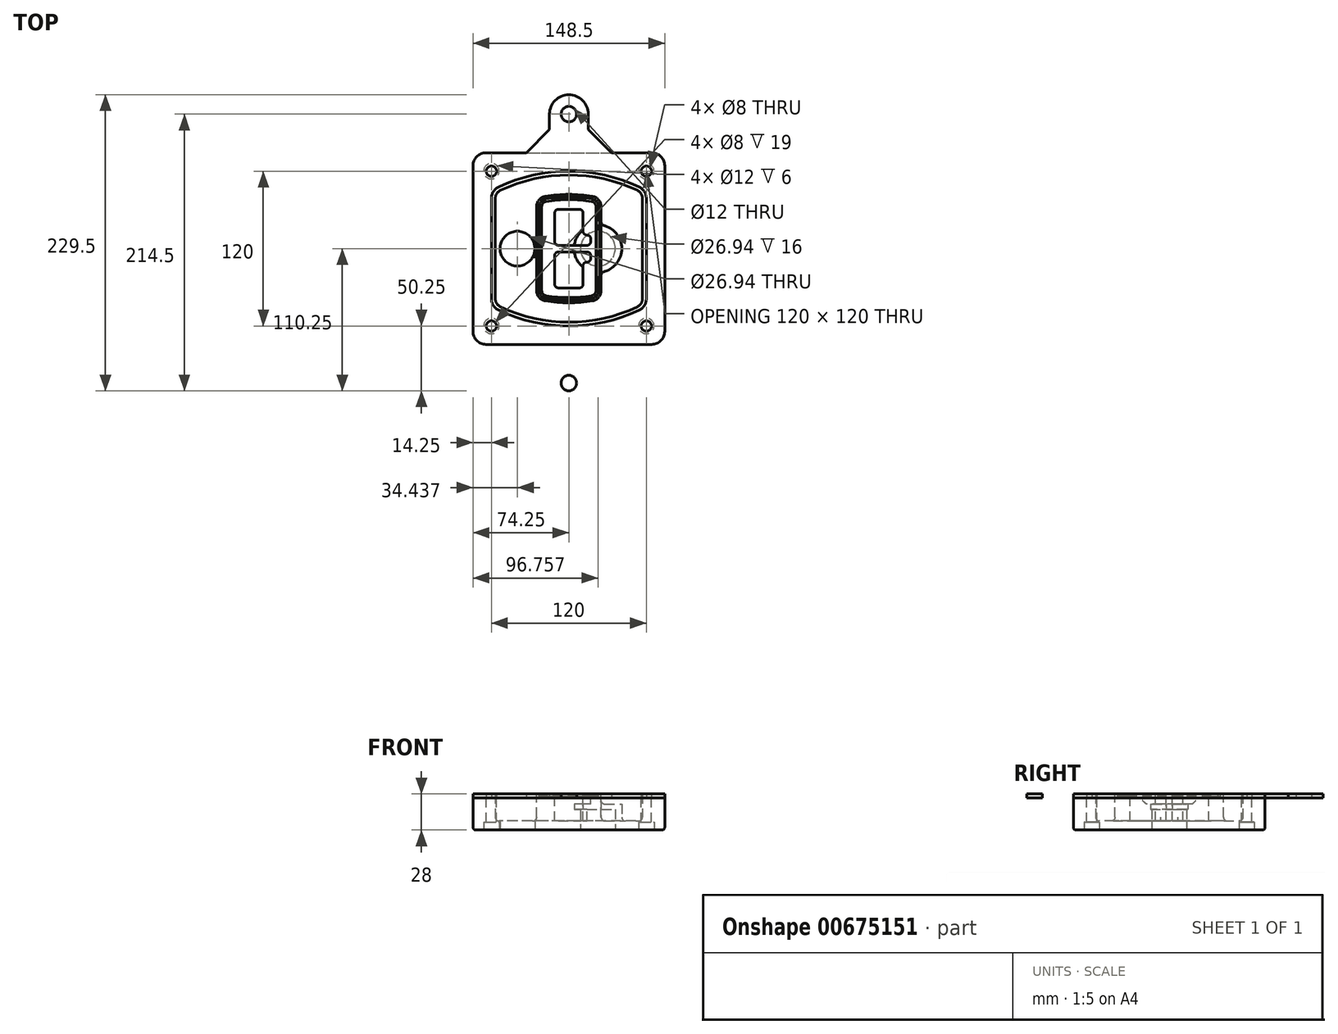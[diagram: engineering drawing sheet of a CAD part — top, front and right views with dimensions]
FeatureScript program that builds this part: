
annotation { "Feature Type Name" : "Feature", "Feature Type Description" : "" }
export const myFeature = defineFeature(function(context is Context, id is Id, definition is map)
    precondition{}
    {
        {
            var Q0;
            Q0=qCreatedBy(makeId("Top.planeOp"),FACE);
            var sketch = newSketch(context, id + "F0", { "sketchPlane" : qUnion([Q0])});
            skPoint(sketch, "E0.rect.middle", {"position": v(0, 0) * mm});
            skLineSegment(sketch, "E1.bottom", {"start": v(-64.25, -74.25) * mm, "end": v(64.25, -74.25) * mm});
            skLineSegment(sketch, "E1.top", {"start": v(-64.25, 74.25) * mm, "end": v(64.25, 74.25) * mm});
            skLineSegment(sketch, "E1.left", {"start": v(-74.25, -64.25) * mm, "end": v(-74.25, 64.25) * mm});
            skLineSegment(sketch, "E1.right", {"start": v(74.25, -64.25) * mm, "end": v(74.25, 64.25) * mm});
            skLineSegment(sketch, "E2", {"start": v(-74.25, 74.25) * mm, "end": v(74.25, -74.25) * mm, "construction": true});
            skLineSegment(sketch, "E3", {"start": v(74.25, 74.25) * mm, "end": v(-74.25, -74.25) * mm, "construction": true});
            skCircle(sketch, "E4", {"center": v(-60, 60) * mm, "radius": 4 * mm});
            skCircle(sketch, "E5", {"center": v(60, 60) * mm, "radius": 4 * mm});
            skCircle(sketch, "E6", {"center": v(60, -60) * mm, "radius": 4 * mm});
            skCircle(sketch, "E7", {"center": v(-60, -60) * mm, "radius": 4 * mm});
            skLineSegment(sketch, "E8", {"start": v(-60, 60) * mm, "end": v(60, 60) * mm, "construction": true});
            skLineSegment(sketch, "E9", {"start": v(60, 60) * mm, "end": v(60, -60) * mm, "construction": true});
            skLineSegment(sketch, "E10", {"start": v(60, -60) * mm, "end": v(-60, -60) * mm, "construction": true});
            skLineSegment(sketch, "E11", {"start": v(-60, -60) * mm, "end": v(-60, 60) * mm, "construction": true});
            skLineSegment(sketch, "E12", {"start": v(-60, 38.83) * mm, "end": v(-60, -38.83) * mm});
            skLineSegment(sketch, "E13", {"start": v(60, 38.83) * mm, "end": v(60, -38.83) * mm});
            skArc(sketch, "E14", {"start": v(54.26, 47.88) * mm, "mid": v(0, 60) * mm, "end": v(-54.26, 47.88) * mm});
            skArc(sketch, "E15", {"start": v(-54.26, -47.88) * mm, "mid": v(0, -60) * mm, "end": v(54.26, -47.88) * mm});
            skLineSegment(sketch, "E16", {"start": v(-60, 0) * mm, "end": v(60, 0) * mm, "construction": true});
            skPoint(sketch, "E17.visualSharp", {"position": v(-60, -45) * mm});
            skArc(sketch, "E17.filletArc", {"start": v(-60, -38.83) * mm, "mid": v(-58.44, -44.2) * mm, "end": v(-54.26, -47.88) * mm});
            skPoint(sketch, "E18.visualSharp", {"position": v(-60, 45) * mm});
            skArc(sketch, "E18.filletArc", {"start": v(-54.26, 47.88) * mm, "mid": v(-58.44, 44.2) * mm, "end": v(-60, 38.83) * mm});
            skPoint(sketch, "E19.visualSharp", {"position": v(60, 45) * mm});
            skArc(sketch, "E19.filletArc", {"start": v(60, 38.83) * mm, "mid": v(58.44, 44.2) * mm, "end": v(54.26, 47.88) * mm});
            skPoint(sketch, "E20.visualSharp", {"position": v(60, -45) * mm});
            skArc(sketch, "E20.filletArc", {"start": v(54.26, -47.88) * mm, "mid": v(58.44, -44.2) * mm, "end": v(60, -38.83) * mm});
            skPoint(sketch, "E21.visualSharp", {"position": v(-74.25, 74.25) * mm});
            skArc(sketch, "E21.filletArc", {"start": v(-64.25, 74.25) * mm, "mid": v(-71.32, 71.32) * mm, "end": v(-74.25, 64.25) * mm});
            skPoint(sketch, "E22.visualSharp", {"position": v(74.25, 74.25) * mm});
            skArc(sketch, "E22.filletArc", {"start": v(74.25, 64.25) * mm, "mid": v(71.32, 71.32) * mm, "end": v(64.25, 74.25) * mm});
            skPoint(sketch, "E23.visualSharp", {"position": v(74.25, -74.25) * mm});
            skArc(sketch, "E23.filletArc", {"start": v(64.25, -74.25) * mm, "mid": v(71.32, -71.32) * mm, "end": v(74.25, -64.25) * mm});
            skPoint(sketch, "E24.visualSharp", {"position": v(-74.25, -74.25) * mm});
            skArc(sketch, "E24.filletArc", {"start": v(-74.25, -64.25) * mm, "mid": v(-71.32, -71.32) * mm, "end": v(-64.25, -74.25) * mm});
            skArc(sketch, "E25.0", {"start": v(57, 38.83) * mm, "mid": v(55.9, 42.58) * mm, "end": v(52.98, 45.17) * mm});
            skLineSegment(sketch, "E25.1", {"start": v(57, 38.83) * mm, "end": v(57, -38.83) * mm});
            skArc(sketch, "E25.2", {"start": v(52.98, -45.17) * mm, "mid": v(55.9, -42.58) * mm, "end": v(57, -38.83) * mm});
            skArc(sketch, "E25.3", {"start": v(-52.98, -45.17) * mm, "mid": v(0, -57) * mm, "end": v(52.98, -45.17) * mm});
            skArc(sketch, "E25.4", {"start": v(-57, -38.83) * mm, "mid": v(-55.9, -42.58) * mm, "end": v(-52.98, -45.17) * mm});
            skArc(sketch, "E25.5", {"start": v(52.98, 45.17) * mm, "mid": v(0, 57) * mm, "end": v(-52.98, 45.17) * mm});
            skLineSegment(sketch, "E25.6", {"start": v(-57, 38.83) * mm, "end": v(-57, -38.83) * mm});
            skArc(sketch, "E25.7", {"start": v(-52.98, 45.17) * mm, "mid": v(-55.9, 42.58) * mm, "end": v(-57, 38.83) * mm});
            skArc(sketch, "E26.0", {"start": v(-55.96, 51.5) * mm, "mid": v(-61.82, 46.33) * mm, "end": v(-64, 38.83) * mm});
            skArc(sketch, "E26.1", {"start": v(55.96, 51.5) * mm, "mid": v(0, 64) * mm, "end": v(-55.96, 51.5) * mm});
            skArc(sketch, "E26.2", {"start": v(64, 38.83) * mm, "mid": v(61.82, 46.33) * mm, "end": v(55.96, 51.5) * mm});
            skLineSegment(sketch, "E26.3", {"start": v(64, 38.83) * mm, "end": v(64, -38.83) * mm});
            skArc(sketch, "E26.4", {"start": v(55.96, -51.5) * mm, "mid": v(61.82, -46.33) * mm, "end": v(64, -38.83) * mm});
            skLineSegment(sketch, "E26.5", {"start": v(-64, 38.83) * mm, "end": v(-64, -38.83) * mm});
            skArc(sketch, "E26.6", {"start": v(-55.96, -51.5) * mm, "mid": v(0, -64) * mm, "end": v(55.96, -51.5) * mm});
            skArc(sketch, "E26.7", {"start": v(-64, -38.83) * mm, "mid": v(-61.82, -46.33) * mm, "end": v(-55.96, -51.5) * mm});
            skSolve(sketch);
        }
        {
            var Q0;
            Q0=makeQuery(id+"F0.imprint","IMPRINT",FACE,{"disambiguationData":[TD([[makeQuery(id+"F0.imprint","IMPRINT",EDGE,{"derivedFrom":sQuery(id+"F0.wireOp",EDGE,"E1.bottom")}),1.0]])]});
            var Q1;
            Q1=makeQuery(id+"F0.imprint","IMPRINT",FACE,{"disambiguationData":[TD([[makeQuery(id+"F0.imprint","IMPRINT",EDGE,{"derivedFrom":sQuery(id+"F0.wireOp",EDGE,"E12")}),1.0]])]});
            var Q2;
            Q2=makeQuery(id+"F0.imprint","IMPRINT",FACE,{"disambiguationData":[TD([[makeQuery(id+"F0.imprint","IMPRINT",EDGE,{"derivedFrom":sQuery(id+"F0.wireOp",EDGE,"E25.0")}),1.0]])]});
            var Q3;
            Q3=makeQuery(id+"F0.imprint","IMPRINT",FACE,{"disambiguationData":[TD([[makeQuery(id+"F0.imprint","IMPRINT",EDGE,{"derivedFrom":sQuery(id+"F0.wireOp",EDGE,"E12")}),-1.0]])]});
            extrude(context, id + "F1", {"entities" : qUnion([Q0, Q1, Q2, Q3]), "oppositeDirection" : true, "depth" : 25 * mm});
        }
        {
            var Q0;
            Q0=makeQuery(id+"F0.imprint","IMPRINT",FACE,{"disambiguationData":[TD([[makeQuery(id+"F0.imprint","IMPRINT",EDGE,{"derivedFrom":sQuery(id+"F0.wireOp",EDGE,"E12")}),1.0]])]});
            extrude(context, id + "F2", {"entities" : qUnion([Q0]), "operationType" : NewBodyOperationType.ADD, "depth" : 3 * mm});
        }
        {
            var Q0;
            Q0=makeQuery(id+"F0.imprint","IMPRINT",FACE,{"disambiguationData":[TD([[makeQuery(id+"F0.imprint","IMPRINT",EDGE,{"derivedFrom":sQuery(id+"F0.wireOp",EDGE,"E25.0")}),1.0]])]});
            extrude(context, id + "F3", {"entities" : qUnion([Q0]), "operationType" : NewBodyOperationType.REMOVE, "oppositeDirection" : true, "depth" : 18 * mm});
        }
        {
            var Q0;
            Q0=makeQuery(id+"F2.opExtrude","CAP_FACE",FACE,{"disambiguationData":[OSD([sQuery(id+"F0.wireOp",EDGE,"E12"),sQuery(id+"F0.wireOp",EDGE,"E13"),sQuery(id+"F0.wireOp",EDGE,"E14"),sQuery(id+"F0.wireOp",EDGE,"E15"),sQuery(id+"F0.wireOp",EDGE,"E17.filletArc"),sQuery(id+"F0.wireOp",EDGE,"E18.filletArc"),sQuery(id+"F0.wireOp",EDGE,"E19.filletArc"),sQuery(id+"F0.wireOp",EDGE,"E20.filletArc"),sQuery(id+"F0.wireOp",EDGE,"E25.0"),sQuery(id+"F0.wireOp",EDGE,"E25.1"),sQuery(id+"F0.wireOp",EDGE,"E25.2"),sQuery(id+"F0.wireOp",EDGE,"E25.3"),sQuery(id+"F0.wireOp",EDGE,"E25.4"),sQuery(id+"F0.wireOp",EDGE,"E25.5"),sQuery(id+"F0.wireOp",EDGE,"E25.6"),sQuery(id+"F0.wireOp",EDGE,"E25.7")])],"isStart":false});
            var sketch = newSketch(context, id + "F4", { "sketchPlane" : qUnion([Q0])});
            skArc(sketch, "E27.0", {"start": v(-18.34, -40.45) * mm, "mid": v(0, -42) * mm, "end": v(18.34, -40.45) * mm});
            skArc(sketch, "E28.0", {"start": v(18.34, 40.45) * mm, "mid": v(0, 42) * mm, "end": v(-18.34, 40.45) * mm});
            skLineSegment(sketch, "E29", {"start": v(-25, 32.57) * mm, "end": v(-25, -32.57) * mm});
            skLineSegment(sketch, "E30", {"start": v(25, 32.57) * mm, "end": v(25, -32.57) * mm});
            skLineSegment(sketch, "E31", {"start": v(-25, 39.1) * mm, "end": v(25, 39.1) * mm, "construction": true});
            skLineSegment(sketch, "E32", {"start": v(-25, -39.1) * mm, "end": v(25, -39.1) * mm, "construction": true});
            skPoint(sketch, "E33.visualSharp", {"position": v(-25, 39.1) * mm});
            skArc(sketch, "E33.filletArc", {"start": v(-18.34, 40.45) * mm, "mid": v(-23.11, 37.73) * mm, "end": v(-25, 32.57) * mm});
            skPoint(sketch, "E34.visualSharp", {"position": v(25, 39.1) * mm});
            skArc(sketch, "E34.filletArc", {"start": v(25, 32.57) * mm, "mid": v(23.11, 37.73) * mm, "end": v(18.34, 40.45) * mm});
            skPoint(sketch, "E35.visualSharp", {"position": v(25, -39.1) * mm});
            skArc(sketch, "E35.filletArc", {"start": v(18.34, -40.45) * mm, "mid": v(23.11, -37.73) * mm, "end": v(25, -32.57) * mm});
            skPoint(sketch, "E36.visualSharp", {"position": v(-25, -39.1) * mm});
            skArc(sketch, "E36.filletArc", {"start": v(-25, -32.57) * mm, "mid": v(-23.11, -37.73) * mm, "end": v(-18.34, -40.45) * mm});
            skArc(sketch, "E37.0", {"start": v(52.98, 45.17) * mm, "mid": v(0, 57) * mm, "end": v(-52.98, 45.17) * mm});
            skArc(sketch, "E37.1", {"start": v(-52.98, 45.17) * mm, "mid": v(-55.9, 42.58) * mm, "end": v(-57, 38.83) * mm});
            skLineSegment(sketch, "E37.2", {"start": v(-57, 38.83) * mm, "end": v(-57, -38.83) * mm});
            skArc(sketch, "E37.3", {"start": v(-57, -38.83) * mm, "mid": v(-55.9, -42.58) * mm, "end": v(-52.98, -45.17) * mm});
            skArc(sketch, "E37.4", {"start": v(-52.98, -45.17) * mm, "mid": v(0, -57) * mm, "end": v(52.98, -45.17) * mm});
            skArc(sketch, "E37.5", {"start": v(52.98, -45.17) * mm, "mid": v(55.9, -42.58) * mm, "end": v(57, -38.83) * mm});
            skLineSegment(sketch, "E37.6", {"start": v(57, 38.83) * mm, "end": v(57, -38.83) * mm});
            skArc(sketch, "E37.7", {"start": v(57, 38.83) * mm, "mid": v(55.9, 42.58) * mm, "end": v(52.98, 45.17) * mm});
            skLineSegment(sketch, "E38.0", {"start": v(23, 32.57) * mm, "end": v(23, -32.57) * mm});
            skArc(sketch, "E38.1", {"start": v(18, -38.48) * mm, "mid": v(21.58, -36.44) * mm, "end": v(23, -32.57) * mm});
            skArc(sketch, "E38.2", {"start": v(-18, -38.48) * mm, "mid": v(0, -40) * mm, "end": v(18, -38.48) * mm});
            skArc(sketch, "E38.3", {"start": v(-23, -32.57) * mm, "mid": v(-21.58, -36.44) * mm, "end": v(-18, -38.48) * mm});
            skLineSegment(sketch, "E38.4", {"start": v(-23, 32.57) * mm, "end": v(-23, -32.57) * mm});
            skArc(sketch, "E38.5", {"start": v(23, 32.57) * mm, "mid": v(21.58, 36.44) * mm, "end": v(18, 38.48) * mm});
            skArc(sketch, "E38.6", {"start": v(-18, 38.48) * mm, "mid": v(-21.58, 36.44) * mm, "end": v(-23, 32.57) * mm});
            skArc(sketch, "E38.7", {"start": v(18, 38.48) * mm, "mid": v(0, 40) * mm, "end": v(-18, 38.48) * mm});
            skArc(sketch, "E39.0", {"start": v(21, 32.57) * mm, "mid": v(20.06, 35.15) * mm, "end": v(17.67, 36.5) * mm});
            skLineSegment(sketch, "E39.1", {"start": v(21, 32.57) * mm, "end": v(21, -32.57) * mm});
            skArc(sketch, "E39.2", {"start": v(17.67, -36.5) * mm, "mid": v(20.06, -35.15) * mm, "end": v(21, -32.57) * mm});
            skArc(sketch, "E39.3", {"start": v(-17.67, -36.5) * mm, "mid": v(0, -38) * mm, "end": v(17.67, -36.5) * mm});
            skArc(sketch, "E39.4", {"start": v(-21, -32.57) * mm, "mid": v(-20.06, -35.15) * mm, "end": v(-17.67, -36.5) * mm});
            skArc(sketch, "E39.5", {"start": v(17.67, 36.5) * mm, "mid": v(0, 38) * mm, "end": v(-17.67, 36.5) * mm});
            skLineSegment(sketch, "E39.6", {"start": v(-21, 32.57) * mm, "end": v(-21, -32.57) * mm});
            skArc(sketch, "E39.7", {"start": v(-17.67, 36.5) * mm, "mid": v(-20.06, 35.15) * mm, "end": v(-21, 32.57) * mm});
            skLineSegment(sketch, "E40", {"start": v(-25, 0) * mm, "end": v(25, 0) * mm, "construction": true});
            skLineSegment(sketch, "E41", {"start": v(-11, 5.5) * mm, "end": v(-11, 27.5) * mm});
            skLineSegment(sketch, "E42", {"start": v(-8, 30.5) * mm, "end": v(8, 30.5) * mm});
            skLineSegment(sketch, "E43", {"start": v(11, 27.5) * mm, "end": v(11, 13.5) * mm});
            skLineSegment(sketch, "E44", {"start": v(14, 10.5) * mm, "end": v(14, 10.5) * mm});
            skLineSegment(sketch, "E45", {"start": v(17, 7.5) * mm, "end": v(17, 5.5) * mm});
            skLineSegment(sketch, "E46", {"start": v(14, 2.5) * mm, "end": v(-8, 2.5) * mm});
            skPoint(sketch, "E47.visualSharp", {"position": v(-11, 30.5) * mm});
            skArc(sketch, "E47.filletArc", {"start": v(-8, 30.5) * mm, "mid": v(-10.12, 29.62) * mm, "end": v(-11, 27.5) * mm});
            skPoint(sketch, "E48.visualSharp", {"position": v(11, 30.5) * mm});
            skArc(sketch, "E48.filletArc", {"start": v(11, 27.5) * mm, "mid": v(10.12, 29.62) * mm, "end": v(8, 30.5) * mm});
            skPoint(sketch, "E49.visualSharp", {"position": v(11, 10.5) * mm});
            skArc(sketch, "E49.filletArc", {"start": v(11, 13.5) * mm, "mid": v(11.88, 11.38) * mm, "end": v(14, 10.5) * mm});
            skPoint(sketch, "E50.visualSharp", {"position": v(17, 10.5) * mm});
            skArc(sketch, "E50.filletArc", {"start": v(17, 7.5) * mm, "mid": v(16.12, 9.62) * mm, "end": v(14, 10.5) * mm});
            skPoint(sketch, "E51.visualSharp", {"position": v(17, 2.5) * mm});
            skArc(sketch, "E51.filletArc", {"start": v(14, 2.5) * mm, "mid": v(16.12, 3.38) * mm, "end": v(17, 5.5) * mm});
            skPoint(sketch, "E52.visualSharp", {"position": v(-11, 2.5) * mm});
            skArc(sketch, "E52.filletArc", {"start": v(-11, 5.5) * mm, "mid": v(-10.12, 3.38) * mm, "end": v(-8, 2.5) * mm});
            skLineSegment(sketch, "E53.0.MirrorCS", {"start": v(14, -2.5) * mm, "end": v(-8, -2.5) * mm});
            skArc(sketch, "E54.0.MirrorCS", {"start": v(-11, -5.5) * mm, "mid": v(-10.12, -3.38) * mm, "end": v(-8, -2.5) * mm});
            skLineSegment(sketch, "E55.0.MirrorCS", {"start": v(-11, -5.5) * mm, "end": v(-11, -27.5) * mm});
            skArc(sketch, "E56.0.MirrorCS", {"start": v(-8, -30.5) * mm, "mid": v(-10.12, -29.62) * mm, "end": v(-11, -27.5) * mm});
            skLineSegment(sketch, "E57.0.MirrorCS", {"start": v(-8, -30.5) * mm, "end": v(8, -30.5) * mm});
            skArc(sketch, "E58.0.MirrorCS", {"start": v(11, -27.5) * mm, "mid": v(10.12, -29.62) * mm, "end": v(8, -30.5) * mm});
            skLineSegment(sketch, "E59.0.MirrorCS", {"start": v(11, -27.5) * mm, "end": v(11, -13.5) * mm});
            skArc(sketch, "E60.0.MirrorCS", {"start": v(11, -13.5) * mm, "mid": v(11.88, -11.38) * mm, "end": v(14, -10.5) * mm});
            skArc(sketch, "E61.0.MirrorCS", {"start": v(17, -7.5) * mm, "mid": v(16.12, -9.62) * mm, "end": v(14, -10.5) * mm});
            skLineSegment(sketch, "E62.0.MirrorCS", {"start": v(17, -7.5) * mm, "end": v(17, -5.5) * mm});
            skArc(sketch, "E63.0.MirrorCS", {"start": v(14, -2.5) * mm, "mid": v(16.12, -3.38) * mm, "end": v(17, -5.5) * mm});
            skSolve(sketch);
        }
        {
            var Q0;
            Q0=makeQuery(id+"F4.imprint","IMPRINT",FACE,{"disambiguationData":[TD([[makeQuery(id+"F4.imprint","IMPRINT",EDGE,{"derivedFrom":sQuery(id+"F4.wireOp",EDGE,"E27.0")}),1.0]])]});
            var Q1;
            Q1=makeQuery(id+"F4.imprint","IMPRINT",FACE,{"disambiguationData":[TD([[makeQuery(id+"F4.imprint","IMPRINT",EDGE,{"derivedFrom":sQuery(id+"F4.wireOp",EDGE,"E38.0")}),-1.0]])]});
            var Q2;
            Q2=makeQuery(id+"F4.imprint","IMPRINT",FACE,{"disambiguationData":[TD([[makeQuery(id+"F4.imprint","IMPRINT",EDGE,{"derivedFrom":sQuery(id+"F4.wireOp",EDGE,"E39.0")}),1.0]])]});
            extrude(context, id + "F5", {"entities" : qUnion([Q0, Q1, Q2]), "operationType" : NewBodyOperationType.ADD, "endBound" : BoundingType.UP_TO_NEXT, "oppositeDirection" : true, "depth" : 25 * mm});
        }
        {
            var Q0;
            Q0=makeQuery(id+"F4.imprint","IMPRINT",FACE,{"disambiguationData":[TD([[makeQuery(id+"F4.imprint","IMPRINT",EDGE,{"derivedFrom":sQuery(id+"F4.wireOp",EDGE,"E38.0")}),-1.0]])]});
            extrude(context, id + "F6", {"entities" : qUnion([Q0]), "operationType" : NewBodyOperationType.REMOVE, "oppositeDirection" : true, "depth" : 2 * mm});
        }
        {
            var Q0;
            Q0=makeQuery(id+"F1.opExtrude","CAP_FACE",FACE,{"disambiguationData":[OSD([sQuery(id+"F0.wireOp",EDGE,"E1.bottom"),sQuery(id+"F0.wireOp",EDGE,"E1.top"),sQuery(id+"F0.wireOp",EDGE,"E1.left"),sQuery(id+"F0.wireOp",EDGE,"E1.right"),sQuery(id+"F0.wireOp",EDGE,"E4"),sQuery(id+"F0.wireOp",EDGE,"E5"),sQuery(id+"F0.wireOp",EDGE,"E6"),sQuery(id+"F0.wireOp",EDGE,"E7"),sQuery(id+"F0.wireOp",EDGE,"E21.filletArc"),sQuery(id+"F0.wireOp",EDGE,"E22.filletArc"),sQuery(id+"F0.wireOp",EDGE,"E23.filletArc"),sQuery(id+"F0.wireOp",EDGE,"E24.filletArc")])],"isStart":false});
            var sketch = newSketch(context, id + "F7", { "sketchPlane" : qUnion([Q0])});
            skCircle(sketch, "E64", {"center": v(22.5, 0) * mm, "radius": 13.47 * mm});
            skCircle(sketch, "E65", {"center": v(-39.81, 0) * mm, "radius": 13.47 * mm});
            skLineSegment(sketch, "E66", {"start": v(74.25, 0) * mm, "end": v(-74.25, 0) * mm});
            skCircle(sketch, "E67", {"center": v(22.5, 0) * mm, "radius": 18.47 * mm});
            skCircle(sketch, "E68", {"center": v(60, -60) * mm, "radius": 6 * mm});
            skCircle(sketch, "E69", {"center": v(-60, -60) * mm, "radius": 6 * mm});
            skCircle(sketch, "E70", {"center": v(-60, 60) * mm, "radius": 6 * mm});
            skCircle(sketch, "E71", {"center": v(60, 60) * mm, "radius": 6 * mm});
            skSolve(sketch);
        }
        {
            var Q0;
            {var subQ1=sQuery(id+"F7.wireOp",EDGE,"E66");var subQ4=sQuery(id+"F7.wireOp",EDGE,"E64");var subQ6=makeQuery(id+"F7.imprint","INTERSECT",VERTEX,{"disambiguationData":[OD(0.0)],"derivedFrom":[subQ4,subQ1]});Q0=makeQuery(id+"F7.imprint","IMPRINT",FACE,{"disambiguationData":[TD([[makeQuery(id+"F7.imprint","IMPRINT",EDGE,{"disambiguationData":[TD([[subQ6,-1.0]])],"derivedFrom":subQ4}),-1.0]])]});}
            var Q1;
            {var subQ0=sQuery(id+"F7.wireOp",EDGE,"E66");var subQ1=sQuery(id+"F7.wireOp",EDGE,"E64");var subQ3=makeQuery(id+"F7.imprint","INTERSECT",VERTEX,{"disambiguationData":[OD(0.0)],"derivedFrom":[subQ1,subQ0]});Q1=makeQuery(id+"F7.imprint","IMPRINT",FACE,{"disambiguationData":[TD([[makeQuery(id+"F7.imprint","IMPRINT",EDGE,{"disambiguationData":[TD([[subQ3,-1.0]])],"derivedFrom":subQ1}),1.0]])]});}
            var Q2;
            {var subQ0=sQuery(id+"F7.wireOp",EDGE,"E66");var subQ1=sQuery(id+"F7.wireOp",EDGE,"E64");var subQ3=makeQuery(id+"F7.imprint","INTERSECT",VERTEX,{"disambiguationData":[OD(0.0)],"derivedFrom":[subQ1,subQ0]});Q2=makeQuery(id+"F7.imprint","IMPRINT",FACE,{"disambiguationData":[TD([[makeQuery(id+"F7.imprint","IMPRINT",EDGE,{"disambiguationData":[TD([[subQ3,1.0]])],"derivedFrom":subQ1}),1.0]])]});}
            var Q3;
            {var subQ1=sQuery(id+"F7.wireOp",EDGE,"E66");var subQ4=sQuery(id+"F7.wireOp",EDGE,"E64");var subQ6=makeQuery(id+"F7.imprint","INTERSECT",VERTEX,{"disambiguationData":[OD(0.0)],"derivedFrom":[subQ4,subQ1]});Q3=makeQuery(id+"F7.imprint","IMPRINT",FACE,{"disambiguationData":[TD([[makeQuery(id+"F7.imprint","IMPRINT",EDGE,{"disambiguationData":[TD([[subQ6,1.0]])],"derivedFrom":subQ4}),-1.0]])]});}
            extrude(context, id + "F8", {"entities" : qUnion([Q0, Q1, Q2, Q3]), "operationType" : NewBodyOperationType.ADD, "oppositeDirection" : true, "depth" : 20 * mm});
        }
        {
            var Q0;
            {var subQ0=sQuery(id+"F7.wireOp",EDGE,"E66");var subQ1=sQuery(id+"F7.wireOp",EDGE,"E64");var subQ3=makeQuery(id+"F7.imprint","INTERSECT",VERTEX,{"disambiguationData":[OD(0.0)],"derivedFrom":[subQ1,subQ0]});Q0=makeQuery(id+"F7.imprint","IMPRINT",FACE,{"disambiguationData":[TD([[makeQuery(id+"F7.imprint","IMPRINT",EDGE,{"disambiguationData":[TD([[subQ3,-1.0]])],"derivedFrom":subQ1}),1.0]])]});}
            var Q1;
            {var subQ0=sQuery(id+"F7.wireOp",EDGE,"E66");var subQ1=sQuery(id+"F7.wireOp",EDGE,"E64");var subQ3=makeQuery(id+"F7.imprint","INTERSECT",VERTEX,{"disambiguationData":[OD(0.0)],"derivedFrom":[subQ1,subQ0]});Q1=makeQuery(id+"F7.imprint","IMPRINT",FACE,{"disambiguationData":[TD([[makeQuery(id+"F7.imprint","IMPRINT",EDGE,{"disambiguationData":[TD([[subQ3,1.0]])],"derivedFrom":subQ1}),1.0]])]});}
            extrude(context, id + "F9", {"entities" : qUnion([Q0, Q1]), "operationType" : NewBodyOperationType.REMOVE, "oppositeDirection" : true, "depth" : 16 * mm});
        }
        {
            var Q0;
            {var subQ0=sQuery(id+"F7.wireOp",EDGE,"E66");var subQ1=sQuery(id+"F7.wireOp",EDGE,"E65");var subQ3=makeQuery(id+"F7.imprint","INTERSECT",VERTEX,{"disambiguationData":[OD(0.0)],"derivedFrom":[subQ1,subQ0]});Q0=makeQuery(id+"F7.imprint","IMPRINT",FACE,{"disambiguationData":[TD([[makeQuery(id+"F7.imprint","IMPRINT",EDGE,{"disambiguationData":[TD([[subQ3,-1.0]])],"derivedFrom":subQ1}),1.0]])]});}
            var Q1;
            {var subQ0=sQuery(id+"F7.wireOp",EDGE,"E66");var subQ1=sQuery(id+"F7.wireOp",EDGE,"E65");var subQ3=makeQuery(id+"F7.imprint","INTERSECT",VERTEX,{"disambiguationData":[OD(0.0)],"derivedFrom":[subQ1,subQ0]});Q1=makeQuery(id+"F7.imprint","IMPRINT",FACE,{"disambiguationData":[TD([[makeQuery(id+"F7.imprint","IMPRINT",EDGE,{"disambiguationData":[TD([[subQ3,1.0]])],"derivedFrom":subQ1}),1.0]])]});}
            extrude(context, id + "F10", {"entities" : qUnion([Q0, Q1]), "operationType" : NewBodyOperationType.REMOVE, "oppositeDirection" : true, "depth" : 25 * mm});
        }
        {
            var Q0;
            Q0=makeQuery(id+"F7.imprint","IMPRINT",FACE,{"disambiguationData":[TD([[makeQuery(id+"F7.imprint","IMPRINT",EDGE,{"derivedFrom":sQuery(id+"F7.wireOp",EDGE,"E68")}),1.0]])]});
            var Q1;
            Q1=makeQuery(id+"F7.imprint","IMPRINT",FACE,{"disambiguationData":[TD([[makeQuery(id+"F7.imprint","IMPRINT",EDGE,{"derivedFrom":makeQuery(id+"F1.opExtrude","CAP_EDGE",EDGE,{"disambiguationData":[OSD([sQuery(id+"F0.wireOp",EDGE,"E5")])],"isStart":false})}),-1.0]])]});
            var Q2;
            Q2=makeQuery(id+"F7.imprint","IMPRINT",FACE,{"disambiguationData":[TD([[makeQuery(id+"F7.imprint","IMPRINT",EDGE,{"derivedFrom":sQuery(id+"F7.wireOp",EDGE,"E69")}),1.0]])]});
            var Q3;
            Q3=makeQuery(id+"F7.imprint","IMPRINT",FACE,{"disambiguationData":[TD([[makeQuery(id+"F7.imprint","IMPRINT",EDGE,{"derivedFrom":makeQuery(id+"F1.opExtrude","CAP_EDGE",EDGE,{"disambiguationData":[OSD([sQuery(id+"F0.wireOp",EDGE,"E4")])],"isStart":false})}),-1.0]])]});
            var Q4;
            Q4=makeQuery(id+"F7.imprint","IMPRINT",FACE,{"disambiguationData":[TD([[makeQuery(id+"F7.imprint","IMPRINT",EDGE,{"derivedFrom":sQuery(id+"F7.wireOp",EDGE,"E70")}),1.0]])]});
            var Q5;
            Q5=makeQuery(id+"F7.imprint","IMPRINT",FACE,{"disambiguationData":[TD([[makeQuery(id+"F7.imprint","IMPRINT",EDGE,{"derivedFrom":makeQuery(id+"F1.opExtrude","CAP_EDGE",EDGE,{"disambiguationData":[OSD([sQuery(id+"F0.wireOp",EDGE,"E7")])],"isStart":false})}),-1.0]])]});
            var Q6;
            Q6=makeQuery(id+"F7.imprint","IMPRINT",FACE,{"disambiguationData":[TD([[makeQuery(id+"F7.imprint","IMPRINT",EDGE,{"derivedFrom":sQuery(id+"F7.wireOp",EDGE,"E71")}),1.0]])]});
            var Q7;
            Q7=makeQuery(id+"F7.imprint","IMPRINT",FACE,{"disambiguationData":[TD([[makeQuery(id+"F7.imprint","IMPRINT",EDGE,{"derivedFrom":makeQuery(id+"F1.opExtrude","CAP_EDGE",EDGE,{"disambiguationData":[OSD([sQuery(id+"F0.wireOp",EDGE,"E6")])],"isStart":false})}),-1.0]])]});
            extrude(context, id + "F11", {"entities" : qUnion([Q0, Q1, Q2, Q3, Q4, Q5, Q6, Q7]), "operationType" : NewBodyOperationType.REMOVE, "oppositeDirection" : true, "depth" : 6 * mm});
        }
        {
            var Q0;
            Q0=makeQuery(id+"F9.boolean.opBoolean","COPY",FACE,{"derivedFrom":makeQuery(id+"F9.opExtrude","CAP_FACE",FACE,{"disambiguationData":[OSD([sQuery(id+"F7.wireOp",EDGE,"E64")])],"isStart":false})});
            var sketch = newSketch(context, id + "F12", { "sketchPlane" : qUnion([Q0])});
            skArc(sketch, "E72.0", {"start": v(11, 14.45) * mm, "mid": v(6.45, 9.13) * mm, "end": v(4.2, 2.5) * mm});
            skArc(sketch, "E72.1", {"start": v(4.2, -2.5) * mm, "mid": v(6.45, -9.13) * mm, "end": v(11, -14.45) * mm});
            skLineSegment(sketch, "E73", {"start": v(4.2, -2.5) * mm, "end": v(14, -2.5) * mm});
            skLineSegment(sketch, "E74.0", {"start": v(14, 2.5) * mm, "end": v(4.2, 2.5) * mm});
            skArc(sketch, "E74.1", {"start": v(14, 2.5) * mm, "mid": v(16.12, 3.38) * mm, "end": v(17, 5.5) * mm});
            skLineSegment(sketch, "E74.2", {"start": v(17, 7.5) * mm, "end": v(17, 5.5) * mm});
            skArc(sketch, "E74.3", {"start": v(17, 7.5) * mm, "mid": v(16.12, 9.62) * mm, "end": v(14, 10.5) * mm});
            skArc(sketch, "E74.4", {"start": v(11, 13.5) * mm, "mid": v(11.88, 11.38) * mm, "end": v(14, 10.5) * mm});
            skLineSegment(sketch, "E74.5", {"start": v(11, 14.45) * mm, "end": v(11, 13.5) * mm});
            skLineSegment(sketch, "E74.7", {"start": v(14, -2.5) * mm, "end": v(4.2, -2.5) * mm});
            skArc(sketch, "E74.8", {"start": v(14, -2.5) * mm, "mid": v(16.12, -3.38) * mm, "end": v(17, -5.5) * mm});
            skLineSegment(sketch, "E74.9", {"start": v(17, -7.5) * mm, "end": v(17, -5.5) * mm});
            skArc(sketch, "E74.10", {"start": v(17, -7.5) * mm, "mid": v(16.12, -9.62) * mm, "end": v(14, -10.5) * mm});
            skArc(sketch, "E74.11", {"start": v(11, -13.5) * mm, "mid": v(11.88, -11.38) * mm, "end": v(14, -10.5) * mm});
            skLineSegment(sketch, "E74.12", {"start": v(11, -14.45) * mm, "end": v(11, -13.5) * mm});
            skPoint(sketch, "E75.orphan", {"position": v(11, -27.5) * mm});
            skPoint(sketch, "E76.orphan", {"position": v(-8, -2.5) * mm});
            skPoint(sketch, "E77.orphan", {"position": v(-8, 2.5) * mm});
            skPoint(sketch, "E78.orphan", {"position": v(11, 27.5) * mm});
            skSolve(sketch);
        }
        {
            var Q0;
            {var subQ7=sQuery(id+"F12.wireOp",EDGE,"E72.0");var subQ14=sQuery(id+"F12.wireOp",EDGE,"E72.1");var subQ16=sQuery(id+"F12.wireOp",EDGE,"E74.1");var subQ18=sQuery(id+"F12.wireOp",EDGE,"E74.8");Q0=qUnion([makeQuery(id+"F12.imprint","IMPRINT",FACE,{"disambiguationData":[TD([[makeQuery(id+"F12.imprint","IMPRINT",EDGE,{"derivedFrom":subQ7}),1.0]])]}),makeQuery(id+"F12.imprint","IMPRINT",FACE,{"disambiguationData":[TD([[makeQuery(id+"F12.imprint","IMPRINT",EDGE,{"derivedFrom":subQ14}),1.0]])]}),makeQuery(id+"F12.imprint","IMPRINT",FACE,{"disambiguationData":[TD([[makeQuery(id+"F12.imprint","IMPRINT",EDGE,{"derivedFrom":subQ16}),1.0]])]}),makeQuery(id+"F12.imprint","IMPRINT",FACE,{"disambiguationData":[TD([[makeQuery(id+"F12.imprint","IMPRINT",EDGE,{"derivedFrom":subQ18}),-1.0]])]})]);}
            var Q1;
            Q1=makeQuery(id+"F5.boolean.opBoolean","SPLIT",FACE,{"disambiguationData":[TD([makeQuery(id+"F5.opExtrude","SWEPT_FACE",FACE,{"disambiguationData":[OSD([sQuery(id+"F4.wireOp",EDGE,"E41")])]})])],"derivedFrom":makeQuery(id+"F3.boolean.opBoolean","COPY",FACE,{"derivedFrom":makeQuery(id+"F3.opExtrude","CAP_FACE",FACE,{"disambiguationData":[OSD([sQuery(id+"F0.wireOp",EDGE,"E25.0"),sQuery(id+"F0.wireOp",EDGE,"E25.1"),sQuery(id+"F0.wireOp",EDGE,"E25.2"),sQuery(id+"F0.wireOp",EDGE,"E25.3"),sQuery(id+"F0.wireOp",EDGE,"E25.4"),sQuery(id+"F0.wireOp",EDGE,"E25.5"),sQuery(id+"F0.wireOp",EDGE,"E25.6"),sQuery(id+"F0.wireOp",EDGE,"E25.7")])],"isStart":false})})});
            extrude(context, id + "F13", {"entities" : qUnion([Q0]), "operationType" : NewBodyOperationType.REMOVE, "endBound" : BoundingType.UP_TO_SURFACE, "endBoundEntityFace" : qUnion([Q1]), "depth" : 25 * mm});
        }
        {
            var Q0;
            Q0=makeQuery(id+"F3.boolean.opBoolean","COPY",EDGE,{"derivedFrom":makeQuery(id+"F3.opExtrude","CAP_EDGE",EDGE,{"disambiguationData":[OSD([sQuery(id+"F0.wireOp",EDGE,"E25.6")])],"isStart":false})});
            var Q1;
            Q1=makeQuery(id+"F8.boolean.opBoolean","INTERSECT",EDGE,{"derivedFrom":[makeQuery(id+"F5.opExtrude","SWEPT_FACE",FACE,{"disambiguationData":[OSD([sQuery(id+"F4.wireOp",EDGE,"E30")])]}),makeQuery(id+"F8.opExtrude","CAP_FACE",FACE,{"disambiguationData":[OSD([sQuery(id+"F7.wireOp",EDGE,"E67")])],"isStart":false})]});
            var Q2;
            Q2=makeQuery(id+"F8.boolean.opBoolean","INTERSECT",EDGE,{"disambiguationData":[OD(1.0)],"derivedFrom":[makeQuery(id+"F5.opExtrude","SWEPT_FACE",FACE,{"disambiguationData":[OSD([sQuery(id+"F4.wireOp",EDGE,"E30")])]}),makeQuery(id+"F8.opExtrude","SWEPT_FACE",FACE,{"disambiguationData":[OSD([sQuery(id+"F7.wireOp",EDGE,"E67")])]})]});
            var Q3;
            {var subQ0=sQuery(id+"F4.wireOp",EDGE,"E30");Q3=makeQuery(id+"F8.boolean.opBoolean","SPLIT",EDGE,{"disambiguationData":[TD([makeQuery(id+"F5.opExtrude","SWEPT_FACE",FACE,{"disambiguationData":[OSD([sQuery(id+"F4.wireOp",EDGE,"E35.filletArc")])]})])],"derivedFrom":makeQuery(id+"F5.opExtrude","CAP_EDGE",EDGE,{"disambiguationData":[OSD([subQ0])],"isStart":false})});}
            var Q4;
            {var subQ0=sQuery(id+"F0.wireOp",EDGE,"E25.7");var subQ1=sQuery(id+"F0.wireOp",EDGE,"E25.1");var subQ2=sQuery(id+"F0.wireOp",EDGE,"E25.6");var subQ3=sQuery(id+"F0.wireOp",EDGE,"E25.5");var subQ4=sQuery(id+"F0.wireOp",EDGE,"E25.4");var subQ5=sQuery(id+"F0.wireOp",EDGE,"E25.0");var subQ6=sQuery(id+"F0.wireOp",EDGE,"E25.2");var subQ7=sQuery(id+"F0.wireOp",EDGE,"E25.3");Q4=makeQuery(id+"F8.boolean.opBoolean","INTERSECT",EDGE,{"derivedFrom":[makeQuery(id+"F5.boolean.opBoolean","SPLIT",FACE,{"disambiguationData":[TD([makeQuery(id+"F2.opExtrude","SWEPT_FACE",FACE,{"disambiguationData":[OSD([subQ5])]})])],"derivedFrom":makeQuery(id+"F3.boolean.opBoolean","COPY",FACE,{"derivedFrom":makeQuery(id+"F3.opExtrude","CAP_FACE",FACE,{"disambiguationData":[OSD([subQ5,subQ1,subQ6,subQ7,subQ4,subQ3,subQ2,subQ0])],"isStart":false})})}),makeQuery(id+"F8.opExtrude","SWEPT_FACE",FACE,{"disambiguationData":[OSD([sQuery(id+"F7.wireOp",EDGE,"E67")])]})]});}
            var Q5;
            Q5=makeQuery(id+"F8.boolean.opBoolean","INTERSECT",EDGE,{"disambiguationData":[OD(0.0)],"derivedFrom":[makeQuery(id+"F5.opExtrude","SWEPT_FACE",FACE,{"disambiguationData":[OSD([sQuery(id+"F4.wireOp",EDGE,"E30")])]}),makeQuery(id+"F8.opExtrude","SWEPT_FACE",FACE,{"disambiguationData":[OSD([sQuery(id+"F7.wireOp",EDGE,"E67")])]})]});
            fillet(context, id + "F14", {"entities" : qUnion([Q0, Q1, Q2, Q3, Q4, Q5]), "radius" : 3 * mm, "tangentPropagation" : true, "allowEdgeOverflow" : false});
        }
        {
            var Q0;
            Q0=makeQuery(id+"F1.opExtrude","CAP_EDGE",EDGE,{"disambiguationData":[OSD([sQuery(id+"F0.wireOp",EDGE,"E1.bottom")])],"isStart":false});
            fillet(context, id + "F15", {"entities" : qUnion([Q0]), "radius" : 2 * mm, "tangentPropagation" : true, "allowEdgeOverflow" : false});
        }
        {
            var Q0;
            {var subQ0=sQuery(id+"F0.wireOp",EDGE,"E21.filletArc");var subQ1=sQuery(id+"F0.wireOp",EDGE,"E7");var subQ2=sQuery(id+"F0.wireOp",EDGE,"E6");var subQ3=sQuery(id+"F0.wireOp",EDGE,"E5");var subQ4=sQuery(id+"F0.wireOp",EDGE,"E4");var subQ5=sQuery(id+"F0.wireOp",EDGE,"E22.filletArc");var subQ6=sQuery(id+"F0.wireOp",EDGE,"E1.bottom");var subQ7=sQuery(id+"F0.wireOp",EDGE,"E1.right");var subQ8=sQuery(id+"F0.wireOp",EDGE,"E1.top");var subQ9=sQuery(id+"F0.wireOp",EDGE,"E1.left");var subQ10=sQuery(id+"F0.wireOp",EDGE,"E23.filletArc");var subQ11=sQuery(id+"F0.wireOp",EDGE,"E24.filletArc");Q0=makeQuery(id+"F2.boolean.opBoolean","SPLIT",FACE,{"disambiguationData":[TD([makeQuery(id+"F1.opExtrude","SWEPT_FACE",FACE,{"disambiguationData":[OSD([subQ6])]})])],"derivedFrom":makeQuery(id+"F1.opExtrude","CAP_FACE",FACE,{"disambiguationData":[OSD([subQ6,subQ8,subQ9,subQ7,subQ4,subQ3,subQ2,subQ1,subQ0,subQ5,subQ10,subQ11])],"isStart":true})});}
            var sketch = newSketch(context, id + "F16", { "sketchPlane" : qUnion([Q0])});
            skLineSegment(sketch, "E79", {"start": v(0, 74.25) * mm, "end": v(0, 104.25) * mm, "construction": true});
            skCircle(sketch, "E80", {"center": v(0, 104.25) * mm, "radius": 6 * mm});
            skArc(sketch, "E81", {"start": v(-15, 104.25) * mm, "mid": v(0, 119.25) * mm, "end": v(15, 104.25) * mm});
            skLineSegment(sketch, "E82", {"start": v(15, 104.25) * mm, "end": v(15, 92.25) * mm});
            skLineSegment(sketch, "E83", {"start": v(-15, 104.25) * mm, "end": v(-15, 92.25) * mm});
            skLineSegment(sketch, "E84", {"start": v(-15, 92.25) * mm, "end": v(-33, 74.25) * mm});
            skLineSegment(sketch, "E85", {"start": v(15, 92.25) * mm, "end": v(33, 74.25) * mm});
            skLineSegment(sketch, "E86", {"start": v(-74.25, 0) * mm, "end": v(74.25, 0) * mm, "construction": true});
            skArc(sketch, "E87.MirrorCS", {"start": v(15, 104.25) * mm, "mid": v(0, 119.25) * mm, "end": v(-15, 104.25) * mm});
            skLineSegment(sketch, "E88.MirrorCS", {"start": v(74.25, 0) * mm, "end": v(-74.25, 0) * mm, "construction": true});
            skLineSegment(sketch, "E89.MirrorCS", {"start": v(0, -74.25) * mm, "end": v(0, -104.25) * mm, "construction": true});
            skCircle(sketch, "E90.MirrorC", {"center": v(0, -104.25) * mm, "radius": 6 * mm});
            skArc(sketch, "E91.MirrorCS", {"start": v(-15, -104.25) * mm, "mid": v(0, -119.25) * mm, "end": v(15, -104.25) * mm});
            skLineSegment(sketch, "E92.MirrorCS", {"start": v(-15, -92.25) * mm, "end": v(-33, -74.25) * mm});
            skLineSegment(sketch, "E93.MirrorCS", {"start": v(15, -104.25) * mm, "end": v(15, -92.25) * mm});
            skLineSegment(sketch, "E94.MirrorCS", {"start": v(-15, -104.25) * mm, "end": v(-15, -92.25) * mm});
            skLineSegment(sketch, "E95.MirrorCS", {"start": v(15, -92.25) * mm, "end": v(33, -74.25) * mm});
            skSolve(sketch);
        }
        {
            var Q0;
            Q0=makeQuery(id+"F16.imprint","IMPRINT",FACE,{"disambiguationData":[TD([[makeQuery(id+"F16.imprint","IMPRINT",EDGE,{"derivedFrom":sQuery(id+"F16.wireOp",EDGE,"E83")}),1.0]])]});
            var sketch = newSketch(context, id + "F17", { "sketchPlane" : qUnion([Q0])});
            skSolve(sketch);
        }
        {
            var Q0;
            Q0=makeQuery(id+"F16.imprint","IMPRINT",FACE,{"disambiguationData":[TD([[makeQuery(id+"F16.imprint","IMPRINT",EDGE,{"derivedFrom":sQuery(id+"F16.wireOp",EDGE,"E83")}),1.0]])]});
            var Q1;
            Q1=makeQuery(id+"F16.imprint","IMPRINT",FACE,{"disambiguationData":[TD([[makeQuery(id+"F16.imprint","IMPRINT",EDGE,{"derivedFrom":makeQuery(id+"F1.opExtrude","CAP_EDGE",EDGE,{"disambiguationData":[OSD([sQuery(id+"F0.wireOp",EDGE,"E1.left")])],"isStart":true})}),-1.0]])]});
            var Q2;
            Q2=makeQuery(id+"F16.imprint","IMPRINT",FACE,{"disambiguationData":[TD([[makeQuery(id+"F16.imprint","IMPRINT",EDGE,{"derivedFrom":sQuery(id+"F16.wireOp",EDGE,"E90.MirrorC")}),1.0]])]});
            var Q3;
            Q3=makeQuery(id+"F2.opExtrude","CAP_FACE",FACE,{"disambiguationData":[OSD([sQuery(id+"F0.wireOp",EDGE,"E12"),sQuery(id+"F0.wireOp",EDGE,"E13"),sQuery(id+"F0.wireOp",EDGE,"E14"),sQuery(id+"F0.wireOp",EDGE,"E15"),sQuery(id+"F0.wireOp",EDGE,"E17.filletArc"),sQuery(id+"F0.wireOp",EDGE,"E18.filletArc"),sQuery(id+"F0.wireOp",EDGE,"E19.filletArc"),sQuery(id+"F0.wireOp",EDGE,"E20.filletArc"),sQuery(id+"F0.wireOp",EDGE,"E25.0"),sQuery(id+"F0.wireOp",EDGE,"E25.1"),sQuery(id+"F0.wireOp",EDGE,"E25.2"),sQuery(id+"F0.wireOp",EDGE,"E25.3"),sQuery(id+"F0.wireOp",EDGE,"E25.4"),sQuery(id+"F0.wireOp",EDGE,"E25.5"),sQuery(id+"F0.wireOp",EDGE,"E25.6"),sQuery(id+"F0.wireOp",EDGE,"E25.7")])],"isStart":false});
            extrude(context, id + "F18", {"entities" : qUnion([Q0, Q1, Q2]), "endBound" : BoundingType.UP_TO_SURFACE, "depth" : 25.4 * mm, "endBoundEntityFace" : qUnion([Q3]), "offsetDistance" : 25.4 * mm});
        }
    });
